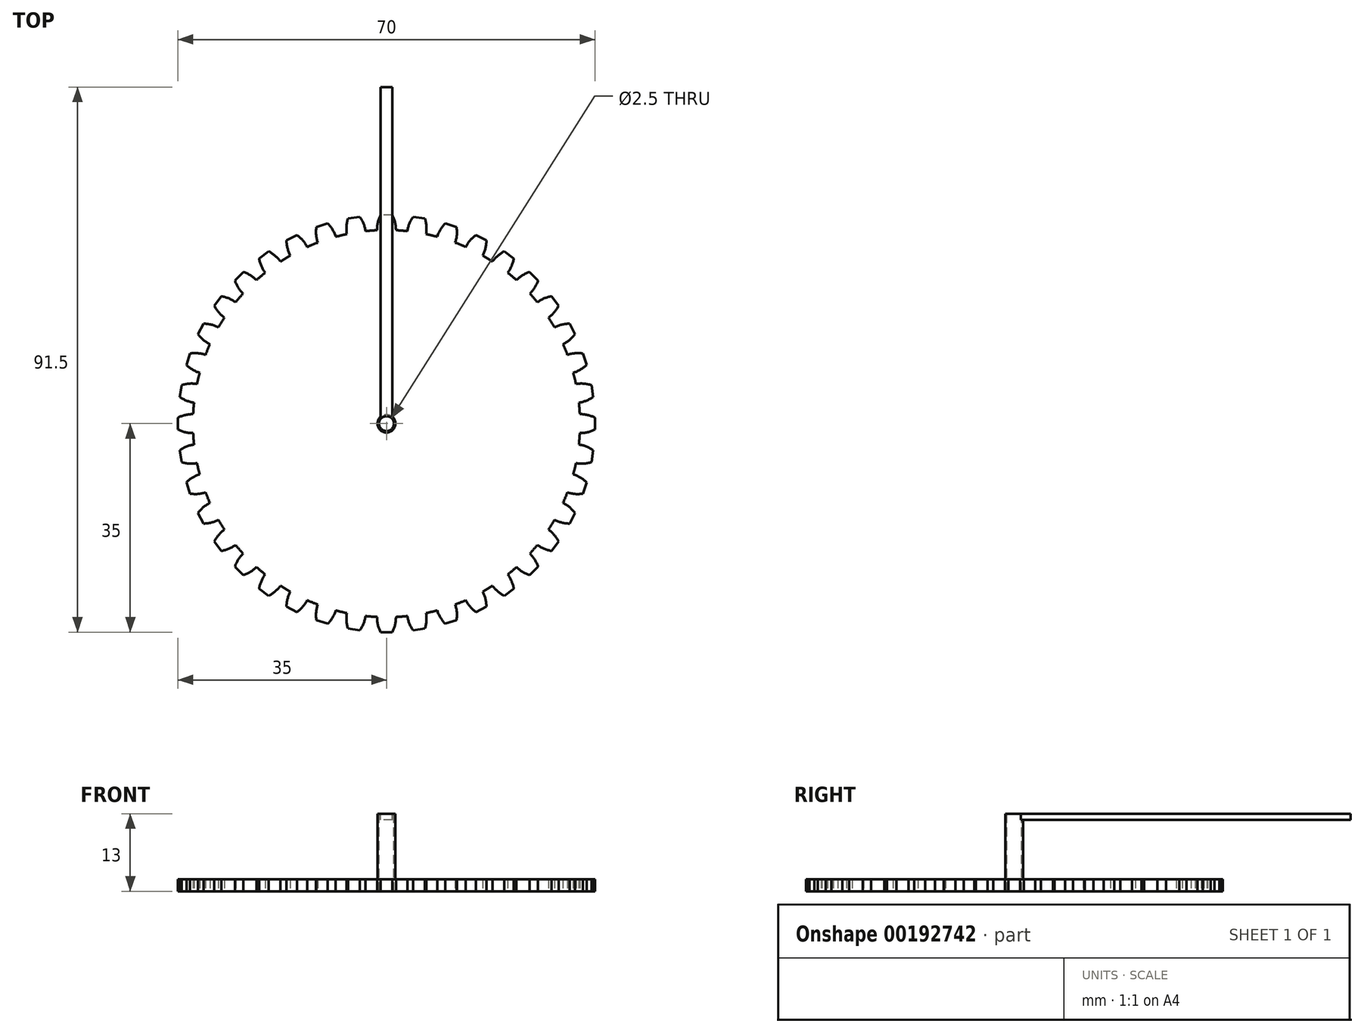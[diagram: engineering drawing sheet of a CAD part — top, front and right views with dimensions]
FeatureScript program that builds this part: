
annotation { "Feature Type Name" : "Feature", "Feature Type Description" : "" }
export const myFeature = defineFeature(function(context is Context, id is Id, definition is map)
    precondition{}
    {
        {
            var Q0;
            Q0=qCreatedBy(makeId("Top.planeOp"),FACE);
            var sketch = newSketch(context, id + "F0", { "sketchPlane" : qUnion([Q0])});
            skCircle(sketch, "E0", {"center": v(0, 0) * mm, "radius": 32.5 * mm});
            skLineSegment(sketch, "E1", {"start": v(0, 0) * mm, "end": v(0, 32.5) * mm, "construction": true});
            skLineSegment(sketch, "E2", {"start": v(0, 35) * mm, "end": v(-1, 35) * mm});
            skArc(sketch, "E3", {"start": v(-1, 35) * mm, "mid": v(-1.45, 33.77) * mm, "end": v(-1.6, 32.46) * mm});
            skLineSegment(sketch, "E4.MirrorCS", {"start": v(0, 35) * mm, "end": v(1, 35) * mm});
            skArc(sketch, "E5.MirrorCS", {"start": v(1, 35) * mm, "mid": v(1.45, 33.77) * mm, "end": v(1.6, 32.46) * mm});
            skArc(sketch, "E6.1.0", {"start": v(-6.46, 34.41) * mm, "mid": v(-6.7, 33.12) * mm, "end": v(-6.65, 31.81) * mm});
            skLineSegment(sketch, "E6.1.1", {"start": v(-5.48, 34.57) * mm, "end": v(-6.46, 34.41) * mm});
            skLineSegment(sketch, "E6.1.2", {"start": v(-5.48, 34.57) * mm, "end": v(-4.49, 34.73) * mm});
            skArc(sketch, "E6.1.3", {"start": v(-4.49, 34.73) * mm, "mid": v(-3.85, 33.58) * mm, "end": v(-3.5, 32.31) * mm});
            skArc(sketch, "E6.2.0", {"start": v(-11.77, 32.98) * mm, "mid": v(-11.8, 31.67) * mm, "end": v(-11.54, 30.38) * mm});
            skLineSegment(sketch, "E6.2.1", {"start": v(-10.82, 33.29) * mm, "end": v(-11.77, 32.98) * mm});
            skLineSegment(sketch, "E6.2.2", {"start": v(-10.82, 33.29) * mm, "end": v(-9.86, 33.6) * mm});
            skArc(sketch, "E6.2.3", {"start": v(-9.86, 33.6) * mm, "mid": v(-9.06, 32.56) * mm, "end": v(-8.52, 31.36) * mm});
            skArc(sketch, "E6.3.0", {"start": v(-16.78, 30.73) * mm, "mid": v(-16.62, 29.43) * mm, "end": v(-16.15, 28.2) * mm});
            skLineSegment(sketch, "E6.3.1", {"start": v(-15.89, 31.19) * mm, "end": v(-16.78, 30.73) * mm});
            skLineSegment(sketch, "E6.3.2", {"start": v(-15.89, 31.19) * mm, "end": v(-15, 31.64) * mm});
            skArc(sketch, "E6.3.3", {"start": v(-15, 31.64) * mm, "mid": v(-14.04, 30.74) * mm, "end": v(-13.32, 29.64) * mm});
            skArc(sketch, "E6.4.0", {"start": v(-21.38, 27.73) * mm, "mid": v(-21.02, 26.47) * mm, "end": v(-20.37, 25.33) * mm});
            skLineSegment(sketch, "E6.4.1", {"start": v(-20.57, 28.32) * mm, "end": v(-21.38, 27.73) * mm});
            skLineSegment(sketch, "E6.4.2", {"start": v(-20.57, 28.32) * mm, "end": v(-19.76, 28.9) * mm});
            skArc(sketch, "E6.4.3", {"start": v(-19.76, 28.9) * mm, "mid": v(-18.68, 28.17) * mm, "end": v(-17.8, 27.2) * mm});
            skArc(sketch, "E6.5.0", {"start": v(-25.46, 24.04) * mm, "mid": v(-24.9, 22.85) * mm, "end": v(-24.08, 21.83) * mm});
            skLineSegment(sketch, "E6.5.1", {"start": v(-24.75, 24.75) * mm, "end": v(-25.46, 24.04) * mm});
            skLineSegment(sketch, "E6.5.2", {"start": v(-24.75, 24.75) * mm, "end": v(-24.04, 25.46) * mm});
            skArc(sketch, "E6.5.3", {"start": v(-24.04, 25.46) * mm, "mid": v(-22.85, 24.9) * mm, "end": v(-21.83, 24.08) * mm});
            skArc(sketch, "E6.6.0", {"start": v(-28.9, 19.76) * mm, "mid": v(-28.17, 18.68) * mm, "end": v(-27.2, 17.8) * mm});
            skLineSegment(sketch, "E6.6.1", {"start": v(-28.32, 20.57) * mm, "end": v(-28.9, 19.76) * mm});
            skLineSegment(sketch, "E6.6.2", {"start": v(-28.32, 20.57) * mm, "end": v(-27.73, 21.38) * mm});
            skArc(sketch, "E6.6.3", {"start": v(-27.73, 21.38) * mm, "mid": v(-26.47, 21.02) * mm, "end": v(-25.33, 20.37) * mm});
            skArc(sketch, "E6.7.0", {"start": v(-31.64, 15) * mm, "mid": v(-30.74, 14.04) * mm, "end": v(-29.64, 13.32) * mm});
            skLineSegment(sketch, "E6.7.1", {"start": v(-31.19, 15.89) * mm, "end": v(-31.64, 15) * mm});
            skLineSegment(sketch, "E6.7.2", {"start": v(-31.19, 15.89) * mm, "end": v(-30.73, 16.78) * mm});
            skArc(sketch, "E6.7.3", {"start": v(-30.73, 16.78) * mm, "mid": v(-29.43, 16.62) * mm, "end": v(-28.2, 16.15) * mm});
            skArc(sketch, "E7.3.8.0", {"start": v(-33.6, 9.86) * mm, "mid": v(-32.56, 9.06) * mm, "end": v(-31.36, 8.52) * mm});
            skLineSegment(sketch, "E7.4.8.0", {"start": v(-33.29, 10.82) * mm, "end": v(-33.6, 9.86) * mm});
            skLineSegment(sketch, "E7.7.8.0", {"start": v(-33.29, 10.82) * mm, "end": v(-32.98, 11.77) * mm});
            skArc(sketch, "E7.10.8.0", {"start": v(-32.98, 11.77) * mm, "mid": v(-31.67, 11.8) * mm, "end": v(-30.38, 11.54) * mm});
            skArc(sketch, "E7.3.9.0", {"start": v(-34.73, 4.49) * mm, "mid": v(-33.58, 3.85) * mm, "end": v(-32.31, 3.5) * mm});
            skLineSegment(sketch, "E7.4.9.0", {"start": v(-34.57, 5.48) * mm, "end": v(-34.73, 4.49) * mm});
            skLineSegment(sketch, "E7.7.9.0", {"start": v(-34.57, 5.48) * mm, "end": v(-34.41, 6.46) * mm});
            skArc(sketch, "E7.10.9.0", {"start": v(-34.41, 6.46) * mm, "mid": v(-33.12, 6.7) * mm, "end": v(-31.81, 6.65) * mm});
            skArc(sketch, "E7.3.10.0", {"start": v(-35, -1) * mm, "mid": v(-33.77, -1.45) * mm, "end": v(-32.46, -1.6) * mm});
            skLineSegment(sketch, "E7.4.10.0", {"start": v(-35, 0) * mm, "end": v(-35, -1) * mm});
            skLineSegment(sketch, "E7.7.10.0", {"start": v(-35, 0) * mm, "end": v(-35, 1) * mm});
            skArc(sketch, "E7.10.10.0", {"start": v(-35, 1) * mm, "mid": v(-33.77, 1.45) * mm, "end": v(-32.46, 1.6) * mm});
            skArc(sketch, "E7.3.11.0", {"start": v(-34.41, -6.46) * mm, "mid": v(-33.12, -6.7) * mm, "end": v(-31.81, -6.65) * mm});
            skLineSegment(sketch, "E7.4.11.0", {"start": v(-34.57, -5.48) * mm, "end": v(-34.41, -6.46) * mm});
            skLineSegment(sketch, "E7.7.11.0", {"start": v(-34.57, -5.48) * mm, "end": v(-34.73, -4.49) * mm});
            skArc(sketch, "E7.10.11.0", {"start": v(-34.73, -4.49) * mm, "mid": v(-33.58, -3.85) * mm, "end": v(-32.31, -3.5) * mm});
            skArc(sketch, "E7.3.12.0", {"start": v(-32.98, -11.77) * mm, "mid": v(-31.67, -11.8) * mm, "end": v(-30.38, -11.54) * mm});
            skLineSegment(sketch, "E7.4.12.0", {"start": v(-33.29, -10.82) * mm, "end": v(-32.98, -11.77) * mm});
            skLineSegment(sketch, "E7.7.12.0", {"start": v(-33.29, -10.82) * mm, "end": v(-33.6, -9.86) * mm});
            skArc(sketch, "E7.10.12.0", {"start": v(-33.6, -9.86) * mm, "mid": v(-32.56, -9.06) * mm, "end": v(-31.36, -8.52) * mm});
            skArc(sketch, "E7.3.13.0", {"start": v(-30.73, -16.78) * mm, "mid": v(-29.43, -16.62) * mm, "end": v(-28.2, -16.15) * mm});
            skLineSegment(sketch, "E7.4.13.0", {"start": v(-31.19, -15.89) * mm, "end": v(-30.73, -16.78) * mm});
            skLineSegment(sketch, "E7.7.13.0", {"start": v(-31.19, -15.89) * mm, "end": v(-31.64, -15) * mm});
            skArc(sketch, "E7.10.13.0", {"start": v(-31.64, -15) * mm, "mid": v(-30.74, -14.04) * mm, "end": v(-29.64, -13.32) * mm});
            skArc(sketch, "E7.3.14.0", {"start": v(-27.73, -21.38) * mm, "mid": v(-26.47, -21.02) * mm, "end": v(-25.33, -20.37) * mm});
            skLineSegment(sketch, "E7.4.14.0", {"start": v(-28.32, -20.57) * mm, "end": v(-27.73, -21.38) * mm});
            skLineSegment(sketch, "E7.7.14.0", {"start": v(-28.32, -20.57) * mm, "end": v(-28.9, -19.76) * mm});
            skArc(sketch, "E7.10.14.0", {"start": v(-28.9, -19.76) * mm, "mid": v(-28.17, -18.68) * mm, "end": v(-27.2, -17.8) * mm});
            skArc(sketch, "E7.3.15.0", {"start": v(-24.04, -25.46) * mm, "mid": v(-22.85, -24.9) * mm, "end": v(-21.83, -24.08) * mm});
            skLineSegment(sketch, "E7.4.15.0", {"start": v(-24.75, -24.75) * mm, "end": v(-24.04, -25.46) * mm});
            skLineSegment(sketch, "E7.7.15.0", {"start": v(-24.75, -24.75) * mm, "end": v(-25.46, -24.04) * mm});
            skArc(sketch, "E7.10.15.0", {"start": v(-25.46, -24.04) * mm, "mid": v(-24.9, -22.85) * mm, "end": v(-24.08, -21.83) * mm});
            skArc(sketch, "E7.3.16.0", {"start": v(-19.76, -28.9) * mm, "mid": v(-18.68, -28.17) * mm, "end": v(-17.8, -27.2) * mm});
            skLineSegment(sketch, "E7.4.16.0", {"start": v(-20.57, -28.32) * mm, "end": v(-19.76, -28.9) * mm});
            skLineSegment(sketch, "E7.7.16.0", {"start": v(-20.57, -28.32) * mm, "end": v(-21.38, -27.73) * mm});
            skArc(sketch, "E7.10.16.0", {"start": v(-21.38, -27.73) * mm, "mid": v(-21.02, -26.47) * mm, "end": v(-20.37, -25.33) * mm});
            skArc(sketch, "E7.3.17.0", {"start": v(-15, -31.64) * mm, "mid": v(-14.04, -30.74) * mm, "end": v(-13.32, -29.64) * mm});
            skLineSegment(sketch, "E7.4.17.0", {"start": v(-15.89, -31.19) * mm, "end": v(-15, -31.64) * mm});
            skLineSegment(sketch, "E7.7.17.0", {"start": v(-15.89, -31.19) * mm, "end": v(-16.78, -30.73) * mm});
            skArc(sketch, "E7.10.17.0", {"start": v(-16.78, -30.73) * mm, "mid": v(-16.62, -29.43) * mm, "end": v(-16.15, -28.2) * mm});
            skArc(sketch, "E7.3.18.0", {"start": v(-9.86, -33.6) * mm, "mid": v(-9.06, -32.56) * mm, "end": v(-8.52, -31.36) * mm});
            skLineSegment(sketch, "E7.4.18.0", {"start": v(-10.82, -33.29) * mm, "end": v(-9.86, -33.6) * mm});
            skLineSegment(sketch, "E7.7.18.0", {"start": v(-10.82, -33.29) * mm, "end": v(-11.77, -32.98) * mm});
            skArc(sketch, "E7.10.18.0", {"start": v(-11.77, -32.98) * mm, "mid": v(-11.8, -31.67) * mm, "end": v(-11.54, -30.38) * mm});
            skArc(sketch, "E7.3.19.0", {"start": v(-4.49, -34.73) * mm, "mid": v(-3.85, -33.58) * mm, "end": v(-3.5, -32.31) * mm});
            skLineSegment(sketch, "E7.4.19.0", {"start": v(-5.48, -34.57) * mm, "end": v(-4.49, -34.73) * mm});
            skLineSegment(sketch, "E7.7.19.0", {"start": v(-5.48, -34.57) * mm, "end": v(-6.46, -34.41) * mm});
            skArc(sketch, "E7.10.19.0", {"start": v(-6.46, -34.41) * mm, "mid": v(-6.7, -33.12) * mm, "end": v(-6.65, -31.81) * mm});
            skArc(sketch, "E7.3.20.0", {"start": v(1, -35) * mm, "mid": v(1.45, -33.77) * mm, "end": v(1.6, -32.46) * mm});
            skLineSegment(sketch, "E7.4.20.0", {"start": v(0, -35) * mm, "end": v(1, -35) * mm});
            skLineSegment(sketch, "E7.7.20.0", {"start": v(0, -35) * mm, "end": v(-1, -35) * mm});
            skArc(sketch, "E7.10.20.0", {"start": v(-1, -35) * mm, "mid": v(-1.45, -33.77) * mm, "end": v(-1.6, -32.46) * mm});
            skArc(sketch, "E7.3.21.0", {"start": v(6.46, -34.41) * mm, "mid": v(6.7, -33.12) * mm, "end": v(6.65, -31.81) * mm});
            skLineSegment(sketch, "E7.4.21.0", {"start": v(5.48, -34.57) * mm, "end": v(6.46, -34.41) * mm});
            skLineSegment(sketch, "E7.7.21.0", {"start": v(5.48, -34.57) * mm, "end": v(4.49, -34.73) * mm});
            skArc(sketch, "E7.10.21.0", {"start": v(4.49, -34.73) * mm, "mid": v(3.85, -33.58) * mm, "end": v(3.5, -32.31) * mm});
            skArc(sketch, "E7.3.22.0", {"start": v(11.77, -32.98) * mm, "mid": v(11.8, -31.67) * mm, "end": v(11.54, -30.38) * mm});
            skLineSegment(sketch, "E7.4.22.0", {"start": v(10.82, -33.29) * mm, "end": v(11.77, -32.98) * mm});
            skLineSegment(sketch, "E7.7.22.0", {"start": v(10.82, -33.29) * mm, "end": v(9.86, -33.6) * mm});
            skArc(sketch, "E7.10.22.0", {"start": v(9.86, -33.6) * mm, "mid": v(9.06, -32.56) * mm, "end": v(8.52, -31.36) * mm});
            skArc(sketch, "E7.3.23.0", {"start": v(16.78, -30.73) * mm, "mid": v(16.62, -29.43) * mm, "end": v(16.15, -28.2) * mm});
            skLineSegment(sketch, "E7.4.23.0", {"start": v(15.89, -31.19) * mm, "end": v(16.78, -30.73) * mm});
            skLineSegment(sketch, "E7.7.23.0", {"start": v(15.89, -31.19) * mm, "end": v(15, -31.64) * mm});
            skArc(sketch, "E7.10.23.0", {"start": v(15, -31.64) * mm, "mid": v(14.04, -30.74) * mm, "end": v(13.32, -29.64) * mm});
            skArc(sketch, "E7.3.24.0", {"start": v(21.38, -27.73) * mm, "mid": v(21.02, -26.47) * mm, "end": v(20.37, -25.33) * mm});
            skLineSegment(sketch, "E7.4.24.0", {"start": v(20.57, -28.32) * mm, "end": v(21.38, -27.73) * mm});
            skLineSegment(sketch, "E7.7.24.0", {"start": v(20.57, -28.32) * mm, "end": v(19.76, -28.9) * mm});
            skArc(sketch, "E7.10.24.0", {"start": v(19.76, -28.9) * mm, "mid": v(18.68, -28.17) * mm, "end": v(17.8, -27.2) * mm});
            skArc(sketch, "E7.3.25.0", {"start": v(25.46, -24.04) * mm, "mid": v(24.9, -22.85) * mm, "end": v(24.08, -21.83) * mm});
            skLineSegment(sketch, "E7.4.25.0", {"start": v(24.75, -24.75) * mm, "end": v(25.46, -24.04) * mm});
            skLineSegment(sketch, "E7.7.25.0", {"start": v(24.75, -24.75) * mm, "end": v(24.04, -25.46) * mm});
            skArc(sketch, "E7.10.25.0", {"start": v(24.04, -25.46) * mm, "mid": v(22.85, -24.9) * mm, "end": v(21.83, -24.08) * mm});
            skArc(sketch, "E7.3.26.0", {"start": v(28.9, -19.76) * mm, "mid": v(28.17, -18.68) * mm, "end": v(27.2, -17.8) * mm});
            skLineSegment(sketch, "E7.4.26.0", {"start": v(28.32, -20.57) * mm, "end": v(28.9, -19.76) * mm});
            skLineSegment(sketch, "E7.7.26.0", {"start": v(28.32, -20.57) * mm, "end": v(27.73, -21.38) * mm});
            skArc(sketch, "E7.10.26.0", {"start": v(27.73, -21.38) * mm, "mid": v(26.47, -21.02) * mm, "end": v(25.33, -20.37) * mm});
            skArc(sketch, "E7.3.27.0", {"start": v(31.64, -15) * mm, "mid": v(30.74, -14.04) * mm, "end": v(29.64, -13.32) * mm});
            skLineSegment(sketch, "E7.4.27.0", {"start": v(31.19, -15.89) * mm, "end": v(31.64, -15) * mm});
            skLineSegment(sketch, "E7.7.27.0", {"start": v(31.19, -15.89) * mm, "end": v(30.73, -16.78) * mm});
            skArc(sketch, "E7.10.27.0", {"start": v(30.73, -16.78) * mm, "mid": v(29.43, -16.62) * mm, "end": v(28.2, -16.15) * mm});
            skArc(sketch, "E7.3.28.0", {"start": v(33.6, -9.86) * mm, "mid": v(32.56, -9.06) * mm, "end": v(31.36, -8.52) * mm});
            skLineSegment(sketch, "E7.4.28.0", {"start": v(33.29, -10.82) * mm, "end": v(33.6, -9.86) * mm});
            skLineSegment(sketch, "E7.7.28.0", {"start": v(33.29, -10.82) * mm, "end": v(32.98, -11.77) * mm});
            skArc(sketch, "E7.10.28.0", {"start": v(32.98, -11.77) * mm, "mid": v(31.67, -11.8) * mm, "end": v(30.38, -11.54) * mm});
            skArc(sketch, "E7.3.29.0", {"start": v(34.73, -4.49) * mm, "mid": v(33.58, -3.85) * mm, "end": v(32.31, -3.5) * mm});
            skLineSegment(sketch, "E7.4.29.0", {"start": v(34.57, -5.48) * mm, "end": v(34.73, -4.49) * mm});
            skLineSegment(sketch, "E7.7.29.0", {"start": v(34.57, -5.48) * mm, "end": v(34.41, -6.46) * mm});
            skArc(sketch, "E7.10.29.0", {"start": v(34.41, -6.46) * mm, "mid": v(33.12, -6.7) * mm, "end": v(31.81, -6.65) * mm});
            skArc(sketch, "E7.3.30.0", {"start": v(35, 1) * mm, "mid": v(33.77, 1.45) * mm, "end": v(32.46, 1.6) * mm});
            skLineSegment(sketch, "E7.4.30.0", {"start": v(35, 0) * mm, "end": v(35, 1) * mm});
            skLineSegment(sketch, "E7.7.30.0", {"start": v(35, 0) * mm, "end": v(35, -1) * mm});
            skArc(sketch, "E7.10.30.0", {"start": v(35, -1) * mm, "mid": v(33.77, -1.45) * mm, "end": v(32.46, -1.6) * mm});
            skArc(sketch, "E7.3.31.0", {"start": v(34.41, 6.46) * mm, "mid": v(33.12, 6.7) * mm, "end": v(31.81, 6.65) * mm});
            skLineSegment(sketch, "E7.4.31.0", {"start": v(34.57, 5.48) * mm, "end": v(34.41, 6.46) * mm});
            skLineSegment(sketch, "E7.7.31.0", {"start": v(34.57, 5.48) * mm, "end": v(34.73, 4.49) * mm});
            skArc(sketch, "E7.10.31.0", {"start": v(34.73, 4.49) * mm, "mid": v(33.58, 3.85) * mm, "end": v(32.31, 3.5) * mm});
            skArc(sketch, "E7.3.32.0", {"start": v(32.98, 11.77) * mm, "mid": v(31.67, 11.8) * mm, "end": v(30.38, 11.54) * mm});
            skLineSegment(sketch, "E7.4.32.0", {"start": v(33.29, 10.82) * mm, "end": v(32.98, 11.77) * mm});
            skLineSegment(sketch, "E7.7.32.0", {"start": v(33.29, 10.82) * mm, "end": v(33.6, 9.86) * mm});
            skArc(sketch, "E7.10.32.0", {"start": v(33.6, 9.86) * mm, "mid": v(32.56, 9.06) * mm, "end": v(31.36, 8.52) * mm});
            skArc(sketch, "E7.3.33.0", {"start": v(30.73, 16.78) * mm, "mid": v(29.43, 16.62) * mm, "end": v(28.2, 16.15) * mm});
            skLineSegment(sketch, "E7.4.33.0", {"start": v(31.19, 15.89) * mm, "end": v(30.73, 16.78) * mm});
            skLineSegment(sketch, "E7.7.33.0", {"start": v(31.19, 15.89) * mm, "end": v(31.64, 15) * mm});
            skArc(sketch, "E7.10.33.0", {"start": v(31.64, 15) * mm, "mid": v(30.74, 14.04) * mm, "end": v(29.64, 13.32) * mm});
            skArc(sketch, "E7.3.34.0", {"start": v(27.73, 21.38) * mm, "mid": v(26.47, 21.02) * mm, "end": v(25.33, 20.37) * mm});
            skLineSegment(sketch, "E7.4.34.0", {"start": v(28.32, 20.57) * mm, "end": v(27.73, 21.38) * mm});
            skLineSegment(sketch, "E7.7.34.0", {"start": v(28.32, 20.57) * mm, "end": v(28.9, 19.76) * mm});
            skArc(sketch, "E7.10.34.0", {"start": v(28.9, 19.76) * mm, "mid": v(28.17, 18.68) * mm, "end": v(27.2, 17.8) * mm});
            skArc(sketch, "E7.3.35.0", {"start": v(24.04, 25.46) * mm, "mid": v(22.85, 24.9) * mm, "end": v(21.83, 24.08) * mm});
            skLineSegment(sketch, "E7.4.35.0", {"start": v(24.75, 24.75) * mm, "end": v(24.04, 25.46) * mm});
            skLineSegment(sketch, "E7.7.35.0", {"start": v(24.75, 24.75) * mm, "end": v(25.46, 24.04) * mm});
            skArc(sketch, "E7.10.35.0", {"start": v(25.46, 24.04) * mm, "mid": v(24.9, 22.85) * mm, "end": v(24.08, 21.83) * mm});
            skArc(sketch, "E7.3.36.0", {"start": v(19.76, 28.9) * mm, "mid": v(18.68, 28.17) * mm, "end": v(17.8, 27.2) * mm});
            skLineSegment(sketch, "E7.4.36.0", {"start": v(20.57, 28.32) * mm, "end": v(19.76, 28.9) * mm});
            skLineSegment(sketch, "E7.7.36.0", {"start": v(20.57, 28.32) * mm, "end": v(21.38, 27.73) * mm});
            skArc(sketch, "E7.10.36.0", {"start": v(21.38, 27.73) * mm, "mid": v(21.02, 26.47) * mm, "end": v(20.37, 25.33) * mm});
            skArc(sketch, "E7.3.37.0", {"start": v(15, 31.64) * mm, "mid": v(14.04, 30.74) * mm, "end": v(13.32, 29.64) * mm});
            skLineSegment(sketch, "E7.4.37.0", {"start": v(15.89, 31.19) * mm, "end": v(15, 31.64) * mm});
            skLineSegment(sketch, "E7.7.37.0", {"start": v(15.89, 31.19) * mm, "end": v(16.78, 30.73) * mm});
            skArc(sketch, "E7.10.37.0", {"start": v(16.78, 30.73) * mm, "mid": v(16.62, 29.43) * mm, "end": v(16.15, 28.2) * mm});
            skArc(sketch, "E7.3.38.0", {"start": v(9.86, 33.6) * mm, "mid": v(9.06, 32.56) * mm, "end": v(8.52, 31.36) * mm});
            skLineSegment(sketch, "E7.4.38.0", {"start": v(10.82, 33.29) * mm, "end": v(9.86, 33.6) * mm});
            skLineSegment(sketch, "E7.7.38.0", {"start": v(10.82, 33.29) * mm, "end": v(11.77, 32.98) * mm});
            skArc(sketch, "E7.10.38.0", {"start": v(11.77, 32.98) * mm, "mid": v(11.8, 31.67) * mm, "end": v(11.54, 30.38) * mm});
            skArc(sketch, "E7.3.39.0", {"start": v(4.49, 34.73) * mm, "mid": v(3.85, 33.58) * mm, "end": v(3.5, 32.31) * mm});
            skLineSegment(sketch, "E7.4.39.0", {"start": v(5.48, 34.57) * mm, "end": v(4.49, 34.73) * mm});
            skLineSegment(sketch, "E7.7.39.0", {"start": v(5.48, 34.57) * mm, "end": v(6.46, 34.41) * mm});
            skArc(sketch, "E7.10.39.0", {"start": v(6.46, 34.41) * mm, "mid": v(6.7, 33.12) * mm, "end": v(6.65, 31.81) * mm});
            skSolve(sketch);
        }
        {
            var Q0;
            Q0=qSketchRegion(id+"F0",true);
            extrude(context, id + "F1", {"entities" : qUnion([Q0]), "depth" : 2 * mm});
        }
        {
            var Q0;
            Q0=makeQuery(id+"F1.opExtrude","CAP_FACE",FACE,{"disambiguationData":[OSD([sQuery(id+"F0.wireOp",EDGE,"E0"),sQuery(id+"F0.wireOp",EDGE,"E2"),sQuery(id+"F0.wireOp",EDGE,"E3"),sQuery(id+"F0.wireOp",EDGE,"E4.MirrorCS"),sQuery(id+"F0.wireOp",EDGE,"E5.MirrorCS"),sQuery(id+"F0.wireOp",EDGE,"E6.1.0"),sQuery(id+"F0.wireOp",EDGE,"E6.1.1"),sQuery(id+"F0.wireOp",EDGE,"E6.1.2"),sQuery(id+"F0.wireOp",EDGE,"E6.1.3"),sQuery(id+"F0.wireOp",EDGE,"E6.2.0"),sQuery(id+"F0.wireOp",EDGE,"E6.2.1"),sQuery(id+"F0.wireOp",EDGE,"E6.2.2"),sQuery(id+"F0.wireOp",EDGE,"E6.2.3"),sQuery(id+"F0.wireOp",EDGE,"E6.3.0"),sQuery(id+"F0.wireOp",EDGE,"E6.3.1"),sQuery(id+"F0.wireOp",EDGE,"E6.3.2"),sQuery(id+"F0.wireOp",EDGE,"E6.3.3"),sQuery(id+"F0.wireOp",EDGE,"E6.4.0"),sQuery(id+"F0.wireOp",EDGE,"E6.4.1"),sQuery(id+"F0.wireOp",EDGE,"E6.4.2"),sQuery(id+"F0.wireOp",EDGE,"E6.4.3"),sQuery(id+"F0.wireOp",EDGE,"E6.5.0"),sQuery(id+"F0.wireOp",EDGE,"E6.5.1"),sQuery(id+"F0.wireOp",EDGE,"E6.5.2"),sQuery(id+"F0.wireOp",EDGE,"E6.5.3"),sQuery(id+"F0.wireOp",EDGE,"E6.6.0"),sQuery(id+"F0.wireOp",EDGE,"E6.6.1"),sQuery(id+"F0.wireOp",EDGE,"E6.6.2"),sQuery(id+"F0.wireOp",EDGE,"E6.6.3"),sQuery(id+"F0.wireOp",EDGE,"E6.7.0"),sQuery(id+"F0.wireOp",EDGE,"E6.7.1"),sQuery(id+"F0.wireOp",EDGE,"E6.7.2"),sQuery(id+"F0.wireOp",EDGE,"E6.7.3"),sQuery(id+"F0.wireOp",EDGE,"E6.8.0"),sQuery(id+"F0.wireOp",EDGE,"E6.8.1"),sQuery(id+"F0.wireOp",EDGE,"E6.8.2"),sQuery(id+"F0.wireOp",EDGE,"E6.8.3"),sQuery(id+"F0.wireOp",EDGE,"E6.9.0"),sQuery(id+"F0.wireOp",EDGE,"E6.9.1"),sQuery(id+"F0.wireOp",EDGE,"E6.9.2"),sQuery(id+"F0.wireOp",EDGE,"E6.9.3"),sQuery(id+"F0.wireOp",EDGE,"E6.10.0"),sQuery(id+"F0.wireOp",EDGE,"E6.10.1"),sQuery(id+"F0.wireOp",EDGE,"E6.10.2"),sQuery(id+"F0.wireOp",EDGE,"E6.10.3"),sQuery(id+"F0.wireOp",EDGE,"E6.11.0"),sQuery(id+"F0.wireOp",EDGE,"E6.11.1"),sQuery(id+"F0.wireOp",EDGE,"E6.11.2"),sQuery(id+"F0.wireOp",EDGE,"E6.11.3"),sQuery(id+"F0.wireOp",EDGE,"E6.12.0"),sQuery(id+"F0.wireOp",EDGE,"E6.12.1"),sQuery(id+"F0.wireOp",EDGE,"E6.12.2"),sQuery(id+"F0.wireOp",EDGE,"E6.12.3"),sQuery(id+"F0.wireOp",EDGE,"E6.13.0"),sQuery(id+"F0.wireOp",EDGE,"E6.13.1"),sQuery(id+"F0.wireOp",EDGE,"E6.13.2"),sQuery(id+"F0.wireOp",EDGE,"E6.13.3"),sQuery(id+"F0.wireOp",EDGE,"E6.14.0"),sQuery(id+"F0.wireOp",EDGE,"E6.14.1"),sQuery(id+"F0.wireOp",EDGE,"E6.14.2"),sQuery(id+"F0.wireOp",EDGE,"E6.14.3"),sQuery(id+"F0.wireOp",EDGE,"E6.15.0"),sQuery(id+"F0.wireOp",EDGE,"E6.15.1"),sQuery(id+"F0.wireOp",EDGE,"E6.15.2"),sQuery(id+"F0.wireOp",EDGE,"E6.15.3")])],"isStart":false});
            var sketch = newSketch(context, id + "F2", { "sketchPlane" : qUnion([Q0])});
            skCircle(sketch, "E8", {"center": v(0, 0) * mm, "radius": 1.5 * mm});
            skSolve(sketch);
        }
        {
            var Q0;
            Q0=qSketchRegion(id+"F2",true);
            extrude(context, id + "F3", {"entities" : qUnion([Q0]), "operationType" : NewBodyOperationType.ADD, "depth" : 11 * mm});
        }
        {
            var Q0;
            Q0=makeQuery(id+"F3.opExtrude","CAP_FACE",FACE,{"disambiguationData":[OSD([sQuery(id+"F2.wireOp",EDGE,"E8")])],"isStart":false});
            var sketch = newSketch(context, id + "F4", { "sketchPlane" : qUnion([Q0])});
            skCircle(sketch, "E9", {"center": v(0, 0) * mm, "radius": 1.25 * mm});
            skSolve(sketch);
        }
        {
            var Q0;
            Q0=qSketchRegion(id+"F4",true);
            extrude(context, id + "F5", {"entities" : qUnion([Q0]), "operationType" : NewBodyOperationType.REMOVE, "oppositeDirection" : true, "depth" : 15 * mm});
        }
        {
            var Q0;
            Q0=makeQuery(id+"F3.opExtrude","CAP_FACE",FACE,{"disambiguationData":[OSD([sQuery(id+"F2.wireOp",EDGE,"E8")])],"isStart":false});
            var sketch = newSketch(context, id + "F6", { "sketchPlane" : qUnion([Q0])});
            skLineSegment(sketch, "E10.bottom", {"start": v(0, 1.5) * mm, "end": v(-1, 1.5) * mm});
            skLineSegment(sketch, "E10.top", {"start": v(0, 56.5) * mm, "end": v(-1, 56.5) * mm});
            skLineSegment(sketch, "E10.left", {"start": v(0, 1.5) * mm, "end": v(0, 56.5) * mm});
            skLineSegment(sketch, "E10.right", {"start": v(-1, 1.5) * mm, "end": v(-1, 56.5) * mm});
            skLineSegment(sketch, "E11.MirrorCS", {"start": v(1, 1.5) * mm, "end": v(1, 56.5) * mm});
            skLineSegment(sketch, "E12.MirrorCS", {"start": v(0, 56.5) * mm, "end": v(1, 56.5) * mm});
            skLineSegment(sketch, "E13.MirrorCS", {"start": v(0, 1.5) * mm, "end": v(1, 1.5) * mm});
            skLineSegment(sketch, "E14", {"start": v(-1, 1.5) * mm, "end": v(-1, 1.12) * mm});
            skLineSegment(sketch, "E15", {"start": v(1, 1.5) * mm, "end": v(1, 1.12) * mm});
            skArc(sketch, "E16", {"start": v(-1, 1.12) * mm, "mid": v(0, 1.5) * mm, "end": v(1, 1.12) * mm});
            skSolve(sketch);
        }
        {
            var Q0;
            Q0=qSketchRegion(id+"F6",true);
            extrude(context, id + "F7", {"entities" : qUnion([Q0]), "operationType" : NewBodyOperationType.ADD, "oppositeDirection" : true, "depth" : 1 * mm});
        }
    });
